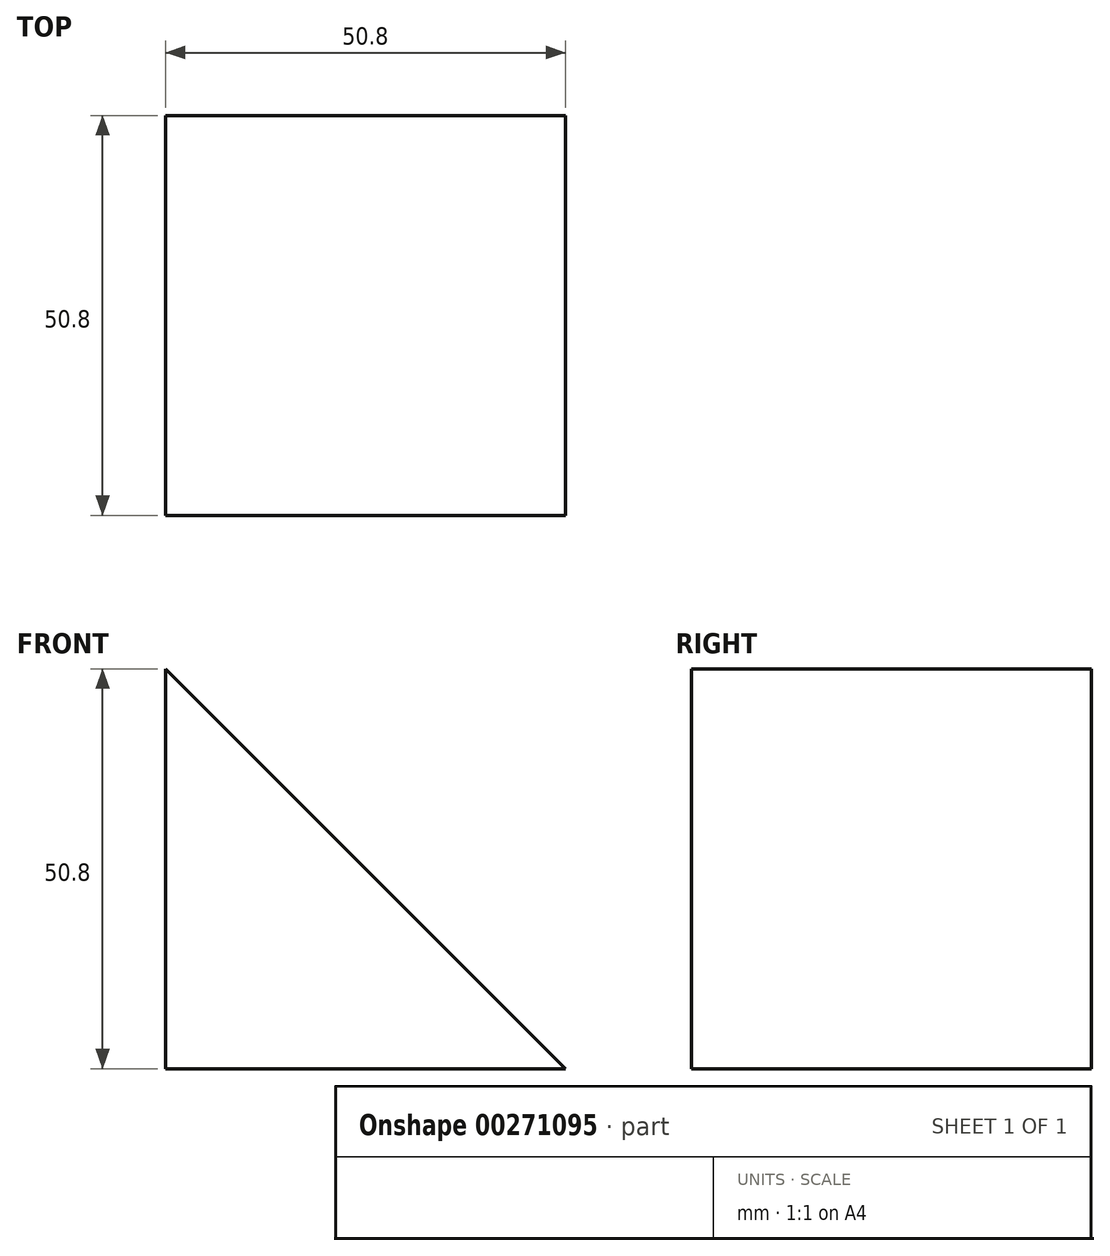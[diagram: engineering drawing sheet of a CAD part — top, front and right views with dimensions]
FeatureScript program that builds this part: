
annotation { "Feature Type Name" : "Feature", "Feature Type Description" : "" }
export const myFeature = defineFeature(function(context is Context, id is Id, definition is map)
    precondition{}
    {
        {
            var Q0;
            Q0=qCreatedBy(makeId("Front.planeOp"),FACE);
            var sketch = newSketch(context, id + "F0", { "sketchPlane" : qUnion([Q0])});
            skLineSegment(sketch, "E0", {"start": v(0, 50.8) * mm, "end": v(0, 0) * mm});
            skLineSegment(sketch, "E1", {"start": v(50.8, 0) * mm, "end": v(0, 0) * mm});
            skLineSegment(sketch, "E2", {"start": v(50.8, 0) * mm, "end": v(0, 50.8) * mm});
            skSolve(sketch);
        }
        {
            var Q0;
            Q0 = qSketchRegion(id + "F0", true);
            extrude(context, id + "F1", {"entities" : qUnion([Q0]), "depth" : 50.8 * mm});
        }
    });
